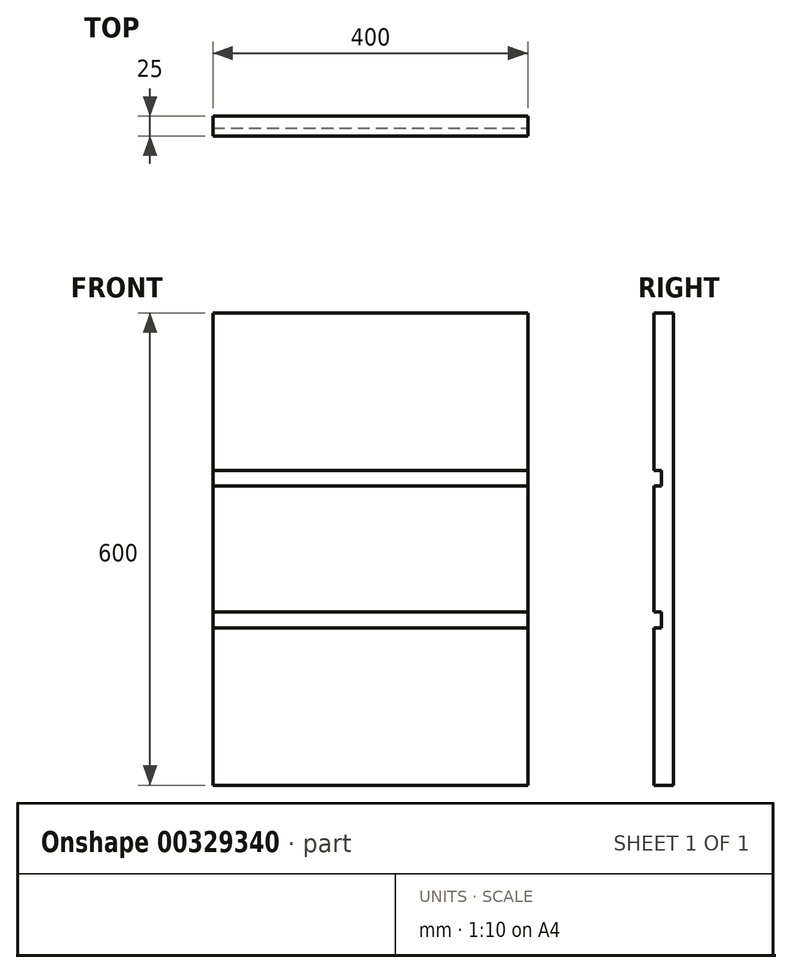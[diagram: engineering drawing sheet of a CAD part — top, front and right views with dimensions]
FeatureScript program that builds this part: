
annotation { "Feature Type Name" : "Feature", "Feature Type Description" : "" }
export const myFeature = defineFeature(function(context is Context, id is Id, definition is map)
    precondition{}
    {
        {
            var Q0;
            Q0=qCreatedBy(makeId("Front.planeOp"),FACE);
            var sketch = newSketch(context, id + "F0", { "sketchPlane" : qUnion([Q0])});
            skLineSegment(sketch, "E0.bottom", {"start": v(0, 0) * mm, "end": v(400, 0) * mm});
            skLineSegment(sketch, "E0.top", {"start": v(0, 600) * mm, "end": v(400, 600) * mm});
            skLineSegment(sketch, "E0.left", {"start": v(0, 0) * mm, "end": v(0, 600) * mm});
            skLineSegment(sketch, "E0.right", {"start": v(400, 0) * mm, "end": v(400, 600) * mm});
            skSolve(sketch);
        }
        {
            var Q0;
            Q0=makeQuery(id+"F0.imprint","IMPRINT",FACE,{"disambiguationData":[TD([[makeQuery(id+"F0.imprint","IMPRINT",EDGE,{"derivedFrom":sQuery(id+"F0.wireOp",EDGE,"E0.bottom")}),1.0]])]});
            var Q1;
            Q1 = qSketchRegion(id + "F0", true);
            extrude(context, id + "F1", {"entities" : qUnion([Q0, Q1]), "depth" : 25 * mm});
        }
        {
            var Q0;
            Q0=makeQuery(id+"F1.opExtrude","CAP_FACE",FACE,{"disambiguationData":[OSD([sQuery(id+"F0.wireOp",EDGE,"E0.bottom"),sQuery(id+"F0.wireOp",EDGE,"E0.top"),sQuery(id+"F0.wireOp",EDGE,"E0.left"),sQuery(id+"F0.wireOp",EDGE,"E0.right")])],"isStart":false});
            var sketch = newSketch(context, id + "F2", { "sketchPlane" : qUnion([Q0])});
            skLineSegment(sketch, "E1.bottom", {"start": v(0, 400) * mm, "end": v(400, 400) * mm});
            skLineSegment(sketch, "E1.top", {"start": v(0, 380) * mm, "end": v(400, 380) * mm});
            skLineSegment(sketch, "E1.left", {"start": v(0, 400) * mm, "end": v(0, 380) * mm});
            skLineSegment(sketch, "E1.right", {"start": v(400, 400) * mm, "end": v(400, 380) * mm});
            skLineSegment(sketch, "E2.bottom", {"start": v(0, 220) * mm, "end": v(400, 220) * mm});
            skLineSegment(sketch, "E2.top", {"start": v(0, 200) * mm, "end": v(400, 200) * mm});
            skLineSegment(sketch, "E2.left", {"start": v(0, 220) * mm, "end": v(0, 200) * mm});
            skLineSegment(sketch, "E2.right", {"start": v(400, 220) * mm, "end": v(400, 200) * mm});
            skSolve(sketch);
        }
        {
            var Q0;
            Q0 = qSketchRegion(id + "F2", true);
            extrude(context, id + "F3", {"entities" : qUnion([Q0]), "operationType" : NewBodyOperationType.REMOVE, "oppositeDirection" : true, "depth" : 10 * mm});
        }
    });
